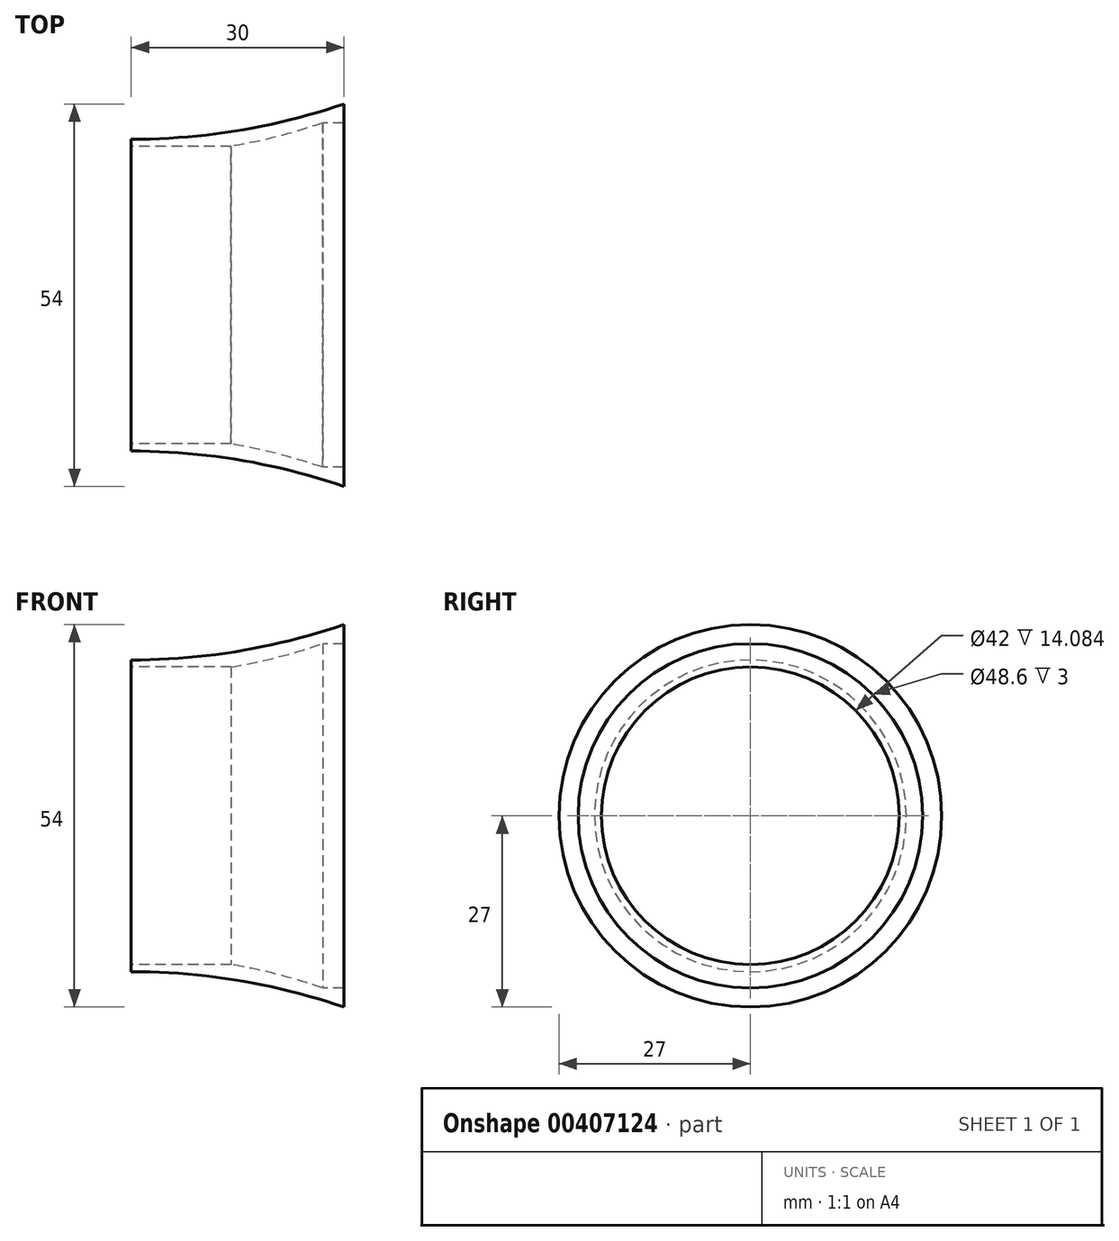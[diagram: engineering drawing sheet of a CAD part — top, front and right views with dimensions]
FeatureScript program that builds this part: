
annotation { "Feature Type Name" : "Feature", "Feature Type Description" : "" }
export const myFeature = defineFeature(function(context is Context, id is Id, definition is map)
    precondition{}
    {
        {
            var Q0;
            Q0=qCreatedBy(makeId("Right.planeOp"),FACE);
            var sketch = newSketch(context, id + "F0", { "sketchPlane" : qUnion([Q0])});
            skCircle(sketch, "E0", {"center": v(0, 0) * mm, "radius": 21 * mm});
            skSolve(sketch);
        }
        {
            var Q0;
            Q0 = qSketchRegion(id + "F0", true);
            extrude(context, id + "F1", {"entities" : qUnion([Q0]), "depth" : 30 * mm, "offsetDistance" : 25 * mm});
        }
        {
            var Q0;
            Q0=qCreatedBy(makeId("Top.planeOp"),FACE);
            var sketch = newSketch(context, id + "F2", { "sketchPlane" : qUnion([Q0])});
            skLineSegment(sketch, "E1", {"start": v(0, 0) * mm, "end": v(30, 0) * mm});
            skLineSegment(sketch, "E2", {"start": v(30, 0) * mm, "end": v(30, 27) * mm});
            skLineSegment(sketch, "E3", {"start": v(30, 27) * mm, "end": v(0, 27) * mm});
            skLineSegment(sketch, "E4", {"start": v(0, 0) * mm, "end": v(0, 27) * mm});
            skLineSegment(sketch, "E5", {"start": v(0, 0) * mm, "end": v(0, 22) * mm});
            skLineSegment(sketch, "E6", {"start": v(0, 22) * mm, "end": v(30, 22) * mm});
            skLineSegment(sketch, "E7", {"start": v(30, 22) * mm, "end": v(30, 27) * mm});
            skArc(sketch, "E8", {"start": v(0, 22) * mm, "mid": v(15.2, 23.26) * mm, "end": v(30, 27) * mm});
            skSolve(sketch);
        }
        {
            var Q0;
            {var subQ2=sQuery(id+"F2.wireOp",EDGE,"E6");Q0=makeQuery(id+"F2.imprint","IMPRINT",FACE,{"disambiguationData":[TD([[makeQuery(id+"F2.imprint","IMPRINT",EDGE,{"derivedFrom":subQ2}),1.0]])]});}
            var Q1;
            {var subQ0=sQuery(id+"F2.wireOp",EDGE,"E1");Q1=makeQuery(id+"F2.imprint","IMPRINT",FACE,{"disambiguationData":[TD([[makeQuery(id+"F2.imprint","IMPRINT",EDGE,{"derivedFrom":subQ0}),1.0]])]});}
            var Q2;
            Q2=sQuery(id+"F2.wireOp",EDGE,"E1");
            revolve(context, id + "F3", {"operationType" : NewBodyOperationType.ADD, "entities" : qUnion([Q0, Q1]), "axis" : qUnion([Q2]), "revolveType" : RevolveType.FULL});
        }
        {
            var Q0;
            Q0=makeQuery(id+"F3.boolean.opBoolean","MERGE",FACE,{"derivedFrom":[makeQuery(id+"F1.opExtrude","CAP_FACE",FACE,{"disambiguationData":[OSD([sQuery(id+"F0.wireOp",EDGE,"E0")])],"isStart":true}),makeQuery(id+"F3.opRevolve","SWEPT_FACE",FACE,{"disambiguationData":[OSD([sQuery(id+"F2.wireOp",EDGE,"E4")])]})]});
            var sketch = newSketch(context, id + "F4", { "sketchPlane" : qUnion([Q0])});
            skCircle(sketch, "E9", {"center": v(0, 0) * mm, "radius": 21 * mm});
            skSolve(sketch);
        }
        {
            var Q0;
            Q0 = qSketchRegion(id + "F4", true);
            extrude(context, id + "F5", {"entities" : qUnion([Q0]), "operationType" : NewBodyOperationType.REMOVE, "oppositeDirection" : true, "depth" : 30 * mm, "offsetDistance" : 25 * mm});
        }
        {
            var Q0;
            Q0=makeQuery(id+"F1.opExtrude","SWEPT_BODY",BODY,{"disambiguationData":[OSD([sQuery(id+"F0.wireOp",EDGE,"E0")])]});
            var Q1;
            Q1=qCreatedBy(makeId("Origin.pointOp"),VERTEX);
            var Q2;
            Q2=qCreatedBy(makeId("Origin.pointOp"),VERTEX);
            transform(context, id + "F6", {"entities" : qUnion([Q0]), "transformType" : TransformType.SCALE_UNIFORMLY, "scale" : 0.9, "scalePoint" : qUnion([Q2]), "makeCopy" : true});
        }
        {
            var Q0;
            Q0=makeQuery(id+"F6.opPattern","COPY",BODY,{"derivedFrom":makeQuery(id+"F1.opExtrude","SWEPT_BODY",BODY,{"disambiguationData":[OSD([sQuery(id+"F0.wireOp",EDGE,"E0")])]}),"instanceName":"1"});
            var Q1;
            Q1=makeQuery(id+"F1.opExtrude","SWEPT_BODY",BODY,{"disambiguationData":[OSD([sQuery(id+"F0.wireOp",EDGE,"E0")])]});
            booleanBodies(context, id + "F7", {"operationType" : BooleanOperationType.SUBTRACTION, "tools" : qUnion([Q0]), "targets" : qUnion([Q1])});
        }
        {
            var Q0;
            Q0=makeQuery(id+"F7.opBoolean","COPY",FACE,{"derivedFrom":makeQuery(id+"F6.opPattern","COPY",FACE,{"derivedFrom":makeQuery(id+"F3.boolean.opBoolean","MERGE",FACE,{"derivedFrom":[makeQuery(id+"F1.opExtrude","CAP_FACE",FACE,{"disambiguationData":[OSD([sQuery(id+"F0.wireOp",EDGE,"E0")])],"isStart":false}),makeQuery(id+"F3.opRevolve","SWEPT_FACE",FACE,{"disambiguationData":[OSD([sQuery(id+"F2.wireOp",EDGE,"E2")])]})]}),"instanceName":"1"})});
            extrude(context, id + "F8", {"entities" : qUnion([Q0]), "operationType" : NewBodyOperationType.REMOVE, "oppositeDirection" : true, "depth" : 25 * mm, "offsetDistance" : 25 * mm});
        }
    });
